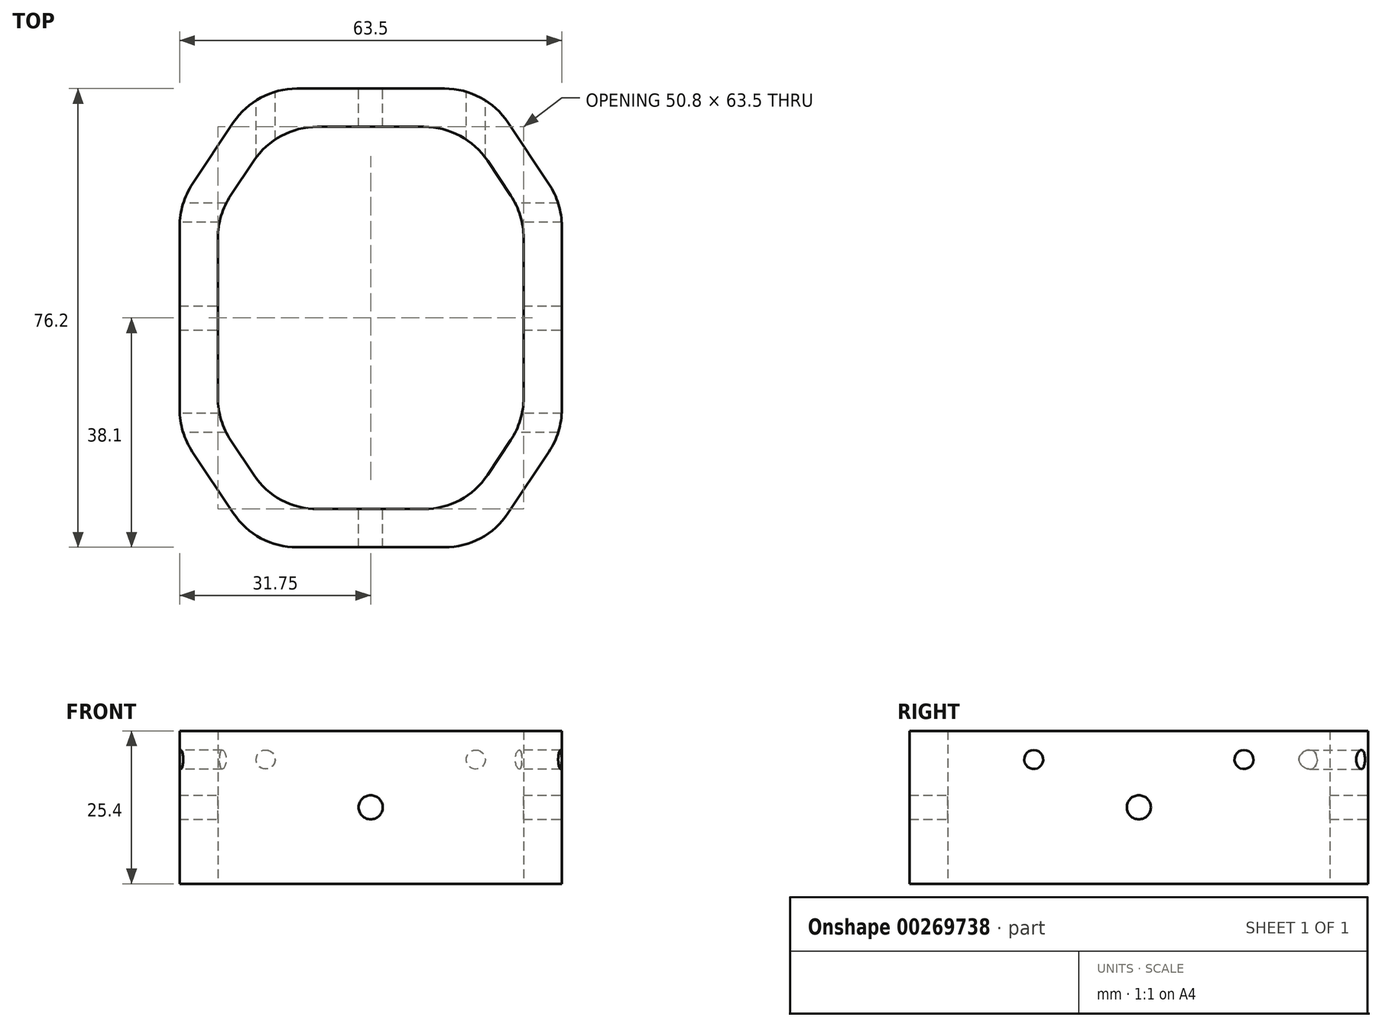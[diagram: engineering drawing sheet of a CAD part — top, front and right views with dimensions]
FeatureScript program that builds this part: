
annotation { "Feature Type Name" : "Feature", "Feature Type Description" : "" }
export const myFeature = defineFeature(function(context is Context, id is Id, definition is map)
    precondition{}
    {
        {
            var Q0;
            Q0=qCreatedBy(makeId("Top.planeOp"),FACE);
            var sketch = newSketch(context, id + "F0", { "sketchPlane" : qUnion([Q0])});
            skLineSegment(sketch, "E0.bottom", {"start": v(19.05, 38.1) * mm, "end": v(-19.05, 38.1) * mm});
            skLineSegment(sketch, "E0.top", {"start": v(19.05, -38.1) * mm, "end": v(-19.05, -38.1) * mm});
            skLineSegment(sketch, "E0.left", {"start": v(31.75, 19.05) * mm, "end": v(31.75, -19.05) * mm});
            skLineSegment(sketch, "E0.right", {"start": v(-31.75, 19.05) * mm, "end": v(-31.75, -19.05) * mm});
            skPoint(sketch, "E0.middle", {"position": v(0, 0) * mm});
            skLineSegment(sketch, "E1", {"start": v(-31.75, 19.05) * mm, "end": v(-19.05, 38.1) * mm});
            skLineSegment(sketch, "E2", {"start": v(19.05, 38.1) * mm, "end": v(31.75, 19.05) * mm});
            skLineSegment(sketch, "E3", {"start": v(31.75, -19.05) * mm, "end": v(19.05, -38.1) * mm});
            skLineSegment(sketch, "E4", {"start": v(-19.05, -38.1) * mm, "end": v(-31.75, -19.05) * mm});
            skLineSegment(sketch, "E5", {"start": v(-25.4, 17.13) * mm, "end": v(-15.65, 31.75) * mm});
            skLineSegment(sketch, "E6", {"start": v(15.65, 31.75) * mm, "end": v(25.4, 17.13) * mm});
            skLineSegment(sketch, "E7", {"start": v(-25.4, -17.13) * mm, "end": v(-15.65, -31.75) * mm});
            skLineSegment(sketch, "E8", {"start": v(15.65, -31.75) * mm, "end": v(25.4, -17.13) * mm});
            skLineSegment(sketch, "E9.trimOffspring", {"start": v(-25.4, 17.13) * mm, "end": v(-25.4, -17.13) * mm});
            skLineSegment(sketch, "E10.trimOffspring", {"start": v(15.65, 31.75) * mm, "end": v(-15.65, 31.75) * mm});
            skLineSegment(sketch, "E11.trimOffspring", {"start": v(25.4, 17.13) * mm, "end": v(25.4, -17.13) * mm});
            skLineSegment(sketch, "E12.trimOffspring", {"start": v(15.65, -31.75) * mm, "end": v(-15.65, -31.75) * mm});
            skSolve(sketch);
        }
        {
            var Q0;
            Q0 = qSketchRegion(id + "F0", true);
            extrude(context, id + "F1", {"entities" : qUnion([Q0]), "depth" : 25.4 * mm});
        }
        {
            var Q0;
            Q0=qCreatedBy(makeId("Front.planeOp"),FACE);
            var sketch = newSketch(context, id + "F2", { "sketchPlane" : qUnion([Q0])});
            skCircle(sketch, "E13", {"center": v(0, 12.7) * mm, "radius": 2 * mm});
            skSolve(sketch);
        }
        {
            var Q0;
            Q0 = qSketchRegion(id + "F2", true);
            extrude(context, id + "F3", {"entities" : qUnion([Q0]), "operationType" : NewBodyOperationType.REMOVE, "endBound" : BoundingType.SYMMETRIC, "depth" : 79.38 * mm});
        }
        {
            var Q0;
            Q0=qCreatedBy(makeId("Right.planeOp"),FACE);
            var sketch = newSketch(context, id + "F4", { "sketchPlane" : qUnion([Q0])});
            skCircle(sketch, "E14", {"center": v(0, 12.7) * mm, "radius": 2 * mm});
            skSolve(sketch);
        }
        {
            var Q0;
            Q0 = qSketchRegion(id + "F4", true);
            extrude(context, id + "F5", {"entities" : qUnion([Q0]), "operationType" : NewBodyOperationType.REMOVE, "endBound" : BoundingType.SYMMETRIC, "oppositeDirection" : true, "depth" : 82.55 * mm});
        }
        {
            var Q0;
            Q0=makeQuery(id+"F1.opExtrude","SWEPT_EDGE",EDGE,{"disambiguationData":[OSD([sQuery(id+"F0.wireOp",EDGE,"E5"),sQuery(id+"F0.wireOp",EDGE,"E9.trimOffspring")])]});
            var Q1;
            Q1=makeQuery(id+"F1.opExtrude","SWEPT_EDGE",EDGE,{"disambiguationData":[OSD([sQuery(id+"F0.wireOp",EDGE,"E5"),sQuery(id+"F0.wireOp",EDGE,"E10.trimOffspring")])]});
            var Q2;
            Q2=makeQuery(id+"F1.opExtrude","SWEPT_EDGE",EDGE,{"disambiguationData":[OSD([sQuery(id+"F0.wireOp",EDGE,"E6"),sQuery(id+"F0.wireOp",EDGE,"E10.trimOffspring")])]});
            var Q3;
            Q3=makeQuery(id+"F1.opExtrude","SWEPT_EDGE",EDGE,{"disambiguationData":[OSD([sQuery(id+"F0.wireOp",EDGE,"E6"),sQuery(id+"F0.wireOp",EDGE,"E11.trimOffspring")])]});
            var Q4;
            Q4=makeQuery(id+"F1.opExtrude","SWEPT_EDGE",EDGE,{"disambiguationData":[OSD([sQuery(id+"F0.wireOp",EDGE,"E8"),sQuery(id+"F0.wireOp",EDGE,"E11.trimOffspring")])]});
            var Q5;
            Q5=makeQuery(id+"F1.opExtrude","SWEPT_EDGE",EDGE,{"disambiguationData":[OSD([sQuery(id+"F0.wireOp",EDGE,"E8"),sQuery(id+"F0.wireOp",EDGE,"E12.trimOffspring")])]});
            var Q6;
            Q6=makeQuery(id+"F1.opExtrude","SWEPT_EDGE",EDGE,{"disambiguationData":[OSD([sQuery(id+"F0.wireOp",EDGE,"E7"),sQuery(id+"F0.wireOp",EDGE,"E12.trimOffspring")])]});
            var Q7;
            Q7=makeQuery(id+"F1.opExtrude","SWEPT_EDGE",EDGE,{"disambiguationData":[OSD([sQuery(id+"F0.wireOp",EDGE,"E7"),sQuery(id+"F0.wireOp",EDGE,"E9.trimOffspring")])]});
            var Q8;
            Q8=makeQuery(id+"F1.opExtrude","SWEPT_EDGE",EDGE,{"disambiguationData":[OSD([sQuery(id+"F0.wireOp",EDGE,"E0.top"),sQuery(id+"F0.wireOp",EDGE,"E4")])]});
            var Q9;
            Q9=makeQuery(id+"F1.opExtrude","SWEPT_EDGE",EDGE,{"disambiguationData":[OSD([sQuery(id+"F0.wireOp",EDGE,"E0.right"),sQuery(id+"F0.wireOp",EDGE,"E4")])]});
            var Q10;
            Q10=makeQuery(id+"F1.opExtrude","SWEPT_EDGE",EDGE,{"disambiguationData":[OSD([sQuery(id+"F0.wireOp",EDGE,"E0.top"),sQuery(id+"F0.wireOp",EDGE,"E3")])]});
            var Q11;
            Q11=makeQuery(id+"F1.opExtrude","SWEPT_EDGE",EDGE,{"disambiguationData":[OSD([sQuery(id+"F0.wireOp",EDGE,"E0.left"),sQuery(id+"F0.wireOp",EDGE,"E3")])]});
            var Q12;
            Q12=makeQuery(id+"F1.opExtrude","SWEPT_EDGE",EDGE,{"disambiguationData":[OSD([sQuery(id+"F0.wireOp",EDGE,"E0.left"),sQuery(id+"F0.wireOp",EDGE,"E2")])]});
            var Q13;
            Q13=makeQuery(id+"F1.opExtrude","SWEPT_EDGE",EDGE,{"disambiguationData":[OSD([sQuery(id+"F0.wireOp",EDGE,"E0.bottom"),sQuery(id+"F0.wireOp",EDGE,"E2")])]});
            var Q14;
            Q14=makeQuery(id+"F1.opExtrude","SWEPT_EDGE",EDGE,{"disambiguationData":[OSD([sQuery(id+"F0.wireOp",EDGE,"E0.bottom"),sQuery(id+"F0.wireOp",EDGE,"E1")])]});
            var Q15;
            Q15=makeQuery(id+"F1.opExtrude","SWEPT_EDGE",EDGE,{"disambiguationData":[OSD([sQuery(id+"F0.wireOp",EDGE,"E0.right"),sQuery(id+"F0.wireOp",EDGE,"E1")])]});
            fillet(context, id + "F6", {"entities" : qUnion([Q0, Q1, Q2, Q3, Q4, Q5, Q6, Q7, Q8, Q9, Q10, Q11, Q12, Q13, Q14, Q15]), "radius" : 12.7 * mm, "tangentPropagation" : true, "allowEdgeOverflow" : false});
        }
        {
            var Q0;
            Q0=makeQuery(id+"F1.opExtrude","SWEPT_FACE",FACE,{"disambiguationData":[OSD([sQuery(id+"F0.wireOp",EDGE,"E0.bottom")])]});
            var sketch = newSketch(context, id + "F7", { "sketchPlane" : qUnion([Q0])});
            skCircle(sketch, "E15", {"center": v(-17.46, 20.64) * mm, "radius": 1.59 * mm});
            skCircle(sketch, "E16", {"center": v(17.46, 20.64) * mm, "radius": 1.59 * mm});
            skSolve(sketch);
        }
        {
            var Q0;
            Q0 = qSketchRegion(id + "F7", true);
            extrude(context, id + "F8", {"entities" : qUnion([Q0]), "operationType" : NewBodyOperationType.REMOVE, "oppositeDirection" : true, "depth" : 25.4 * mm});
        }
        {
            var Q0;
            Q0=qCreatedBy(makeId("Right.planeOp"),FACE);
            var sketch = newSketch(context, id + "F9", { "sketchPlane" : qUnion([Q0])});
            skPoint(sketch, "E17", {"position": v(-17.46, 20.64) * mm});
            skPoint(sketch, "E18", {"position": v(17.46, 20.64) * mm});
            skCircle(sketch, "E19", {"center": v(-17.46, 20.64) * mm, "radius": 1.59 * mm});
            skCircle(sketch, "E20", {"center": v(17.46, 20.64) * mm, "radius": 1.59 * mm});
            skSolve(sketch);
        }
        {
            var Q0;
            Q0 = qSketchRegion(id + "F9", true);
            extrude(context, id + "F10", {"entities" : qUnion([Q0]), "operationType" : NewBodyOperationType.REMOVE, "endBound" : BoundingType.SYMMETRIC, "depth" : 76.2 * mm});
        }
    });
